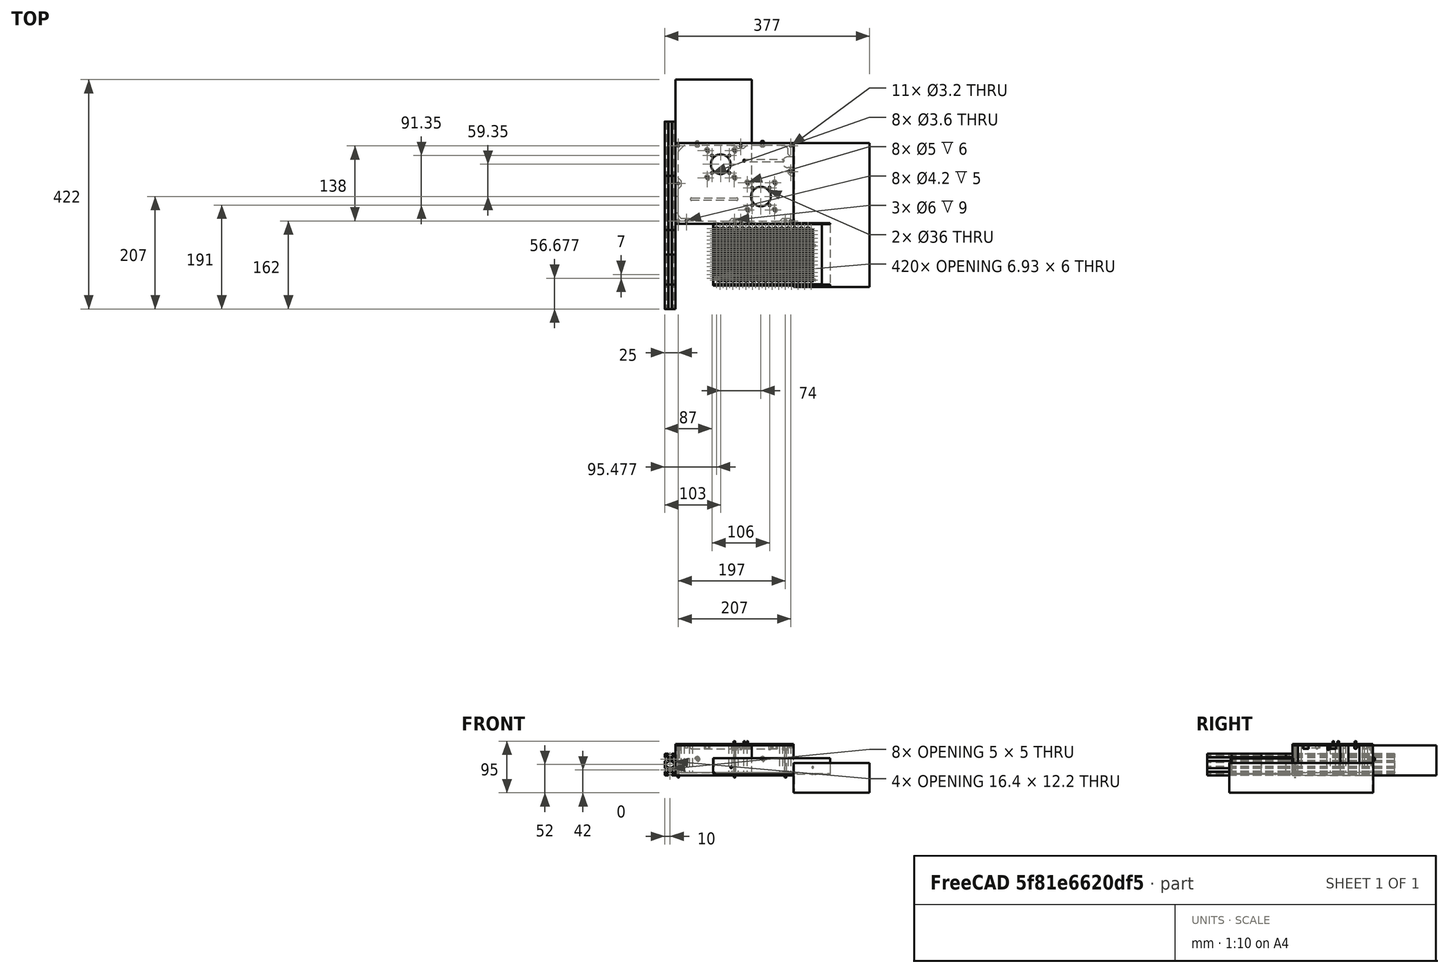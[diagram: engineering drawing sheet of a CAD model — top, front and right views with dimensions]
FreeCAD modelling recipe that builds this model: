
FCSTD DOCUMENT  (FreeCAD 0.19R24291 (Git))
Label: Electronics Enclosure
License: All rights reserved
LicenseURL: http://en.wikipedia.org/wiki/All_rights_reserved
objects: Mesh::Feature×26, Sketcher::SketchObject×10, Part::FeaturePython×10, App::DocumentObjectGroup×6, PartDesign::Pad×5, PartDesign::Pocket×5, Part::Feature×5, PartDesign::Body×3, PartDesign::ShapeBinder×1, Part::Thickness×1, PartDesign::Fillet×1, App::LinkGroup×1
note: 52 computed .brp shape members not serialized (recipe doc carries the construction recipe); baked Part::Feature solids carry a one-line shape summary decoded from their .brp

FEATURE [Sketcher::SketchObject] Sketch
  FullyConstrained = true
  MapMode = 5
  Support = -> [XY_Plane]
  sketch-geometry (8):
    g0: LineSegment StartX=0 StartY=0 StartZ=0 EndX=217 EndY=0 EndZ=0
    g1: LineSegment StartX=217 StartY=0 StartZ=0 EndX=217 EndY=103 EndZ=0
    g2: LineSegment StartX=217 StartY=148 StartZ=0 EndX=0 EndY=148 EndZ=0
    g3: LineSegment StartX=0 StartY=148 StartZ=0 EndX=0 EndY=0 EndZ=0
    g4: LineSegment StartX=217 StartY=123 StartZ=0 EndX=207 EndY=123 EndZ=0
    g5: LineSegment StartX=217 StartY=103 StartZ=0 EndX=207 EndY=103 EndZ=0
    g6: ArcOfCircle CenterX=207 CenterY=113 CenterZ=0 NormalX=0 NormalY=0 NormalZ=1 AngleXU=0 Radius=10 StartAngle=1.5708 EndAngle=4.71239
    g7: LineSegment StartX=217 StartY=123 StartZ=0 EndX=217 EndY=148 EndZ=0
  constraints (23):
    c: Coincident(g0,g1)
    c: Coincident(g7,g2)
    c: Coincident(g2,g3)
    c: Coincident(g3,g0)
    c: Horizontal(g0)
    c: Horizontal(g2)
    c: Vertical(g1)
    c: Vertical(g3)
    c: Coincident(g0,g-1)
    c: DistanceX(g0,g0) = 217
    c: DistanceY(g3,g3) = 148
    c: Horizontal(g4)
    c: Horizontal(g5)
    c: Coincident(g6,g4)
    c: Coincident(g6,g5)
    c: DistanceY(g5,g4) = 20
    c: Vertical(g4,g6)
    c: Vertical(g6,g5)
    c: DistanceY(g4,g7) = 25
    c: DistanceX(g5,g5) = 10
    c: Coincident(g1,g5)
    c: Coincident(g7,g4)
    c: Tangent(g1,g7)
FEATURE [PartDesign::Pad] Pad  label="Base"
  Direction = (1,1,1)
  Length = 5
  Length2 = 100
  Profile = -> Sketch
  Type = 0
FEATURE [Sketcher::SketchObject] Sketch001
  ExternalGeometry = -> [Pad]
  FullyConstrained = true
  MapMode = 5
  Placement = pos=(0,0,5) rot=(0,0,1;0rad)
  Support = -> [Pad]
  sketch-geometry (14):
    g0: LineSegment StartX=217 StartY=10 StartZ=0 EndX=217 EndY=0 EndZ=0
    g1: LineSegment StartX=217 StartY=0 StartZ=0 EndX=0 EndY=0 EndZ=0
    g2: LineSegment StartX=0 StartY=0 StartZ=0 EndX=0 EndY=148 EndZ=0
    g3: LineSegment StartX=0 StartY=148 StartZ=0 EndX=217 EndY=148 EndZ=0
    g4: LineSegment StartX=217 StartY=148 StartZ=0 EndX=217 EndY=123 EndZ=0
    g5: LineSegment StartX=217 StartY=123 StartZ=0 EndX=207 EndY=123 EndZ=0
    g6: LineSegment StartX=207 StartY=123 StartZ=0 EndX=207 EndY=138 EndZ=0
    g7: LineSegment StartX=207 StartY=138 StartZ=0 EndX=10 EndY=138 EndZ=0
    g8: LineSegment StartX=10 StartY=138 StartZ=0 EndX=10 EndY=10 EndZ=0
    g9: LineSegment StartX=10 StartY=10 StartZ=0 EndX=217 EndY=10 EndZ=0
    g10: LineSegment StartX=217 StartY=103 StartZ=0 EndX=207 EndY=103 EndZ=0
    g11: LineSegment StartX=207 StartY=103 StartZ=0 EndX=207 EndY=88 EndZ=0
    g12: LineSegment StartX=207 StartY=88 StartZ=0 EndX=217 EndY=88 EndZ=0
    g13: LineSegment StartX=217 StartY=88 StartZ=0 EndX=217 EndY=103 EndZ=0
  constraints (35):
    c: PointOnObject(g0,g-6)
    c: Coincident(g0,g-6)
    c: Coincident(g0,g1)
    c: Coincident(g1,g-1)
    c: Coincident(g1,g2)
    c: Coincident(g2,g-4)
    c: Coincident(g2,g3)
    c: Coincident(g3,g-4)
    c: Coincident(g3,g4)
    c: Coincident(g4,g-3)
    c: Coincident(g4,g5)
    c: Coincident(g5,g-3)
    c: Coincident(g5,g6)
    c: Vertical(g6)
    c: Coincident(g6,g7)
    c: Horizontal(g7)
    c: Coincident(g7,g8)
    c: Vertical(g8)
    c: Coincident(g8,g9)
    c: Coincident(g9,g0)
    c: Horizontal(g9)
    c: DistanceY(g0,g0) = 10
    c: DistanceY(g6,g3) = 10
    c: DistanceX(g2,g7) = 10
    c: Coincident(g10,g11)
    c: Coincident(g11,g12)
    c: Coincident(g12,g13)
    c: Coincident(g13,g10)
    c: Horizontal(g10)
    c: Horizontal(g12)
    c: Vertical(g11)
    c: Vertical(g13)
    c: Coincident(g10,g-6)
    c: Vertical(g10,g5)
    c: DistanceY(g13,g13) = 15
FEATURE [PartDesign::Pad] Pad001  label="Walls"
  BaseFeature = -> Pad
  Direction = (1,1,1)
  Length = 50
  Length2 = 100
  Profile = -> Sketch001
  Type = 0
FEATURE [Sketcher::SketchObject] Sketch002
  ExternalGeometry = -> [Pad001]
  FullyConstrained = true
  MapMode = 5
  Placement = pos=(0,0,55) rot=(0,0,1;0rad)
  Support = -> [Pad001]
  sketch-geometry (3):
    g0: Circle CenterX=5 CenterY=5 CenterZ=0 NormalX=0 NormalY=0 NormalZ=1 AngleXU=0 Radius=1.6
    g1: Circle CenterX=108.5 CenterY=5 CenterZ=0 NormalX=0 NormalY=0 NormalZ=1 AngleXU=0 Radius=1.6
    g2: Circle CenterX=202 CenterY=5 CenterZ=0 NormalX=0 NormalY=0 NormalZ=1 AngleXU=0 Radius=1.6
  constraints (10):
    c: Horizontal(g0,g1)
    c: Horizontal(g1,g2)
    c: Radius(g0) = 1.6
    c: Equal(g0,g1)
    c: Equal(g1,g2)
    c: DistanceY(g-1,g0) = 5
    c: DistanceX(g-1,g0) = 5
    c: DistanceX(g2,g-3) = 5
    c: DistanceX(g-1,g1) = 108.5
    c: DistanceX(g1,g-3) = 98.5
FEATURE [PartDesign::Pocket] Pocket  label="Center mounting holes"
  BaseFeature = -> Pad001
  Length = 55
  Length2 = 100
  Profile = -> Sketch002
  Type = 0
FEATURE [Sketcher::SketchObject] Sketch003
  ExternalGeometry = -> [Pocket]
  FullyConstrained = true
  MapMode = 5
  Placement = pos=(0,0,55) rot=(0,0,1;0rad)
  Support = -> [Pocket]
  sketch-geometry (3):
    g0: Circle CenterX=5 CenterY=5 CenterZ=0 NormalX=0 NormalY=0 NormalZ=1 AngleXU=0 Radius=3
    g1: Circle CenterX=108.5 CenterY=5 CenterZ=0 NormalX=0 NormalY=0 NormalZ=1 AngleXU=0 Radius=3
    g2: Circle CenterX=202 CenterY=5 CenterZ=0 NormalX=0 NormalY=0 NormalZ=1 AngleXU=0 Radius=3
  constraints (6):
    c: Coincident(g0,g-3)
    c: Coincident(g1,g-4)
    c: Coincident(g2,g-5)
    c: Radius(g0) = 3
    c: Equal(g0,g1)
    c: Equal(g1,g2)
FEATURE [PartDesign::Pocket] Pocket001  label="Center Recess"
  BaseFeature = -> Pocket
  Length = 9
  Length2 = 100
  Profile = -> Sketch003
  Type = 0
FEATURE [Mesh::Feature] _040_Profile___200mm  label="4040_Profile_-_200mm"
  Placement = pos=(8.9e-15,148,40) rot=(0,1,0;1.5708rad)
FEATURE [Sketcher::SketchObject] Sketch004
  FullyConstrained = true
  MapMode = 5
  Placement = pos=(0,138,0) rot=(1,0,0;1.5708rad)
  Support = -> [Pocket001]
  sketch-geometry (2):
    g0: Circle CenterX=40 CenterY=30 CenterZ=0 NormalX=0 NormalY=0 NormalZ=1 AngleXU=0 Radius=2.6
    g1: Circle CenterX=160 CenterY=30 CenterZ=0 NormalX=0 NormalY=0 NormalZ=1 AngleXU=0 Radius=2.6
  constraints (6):
    c: Radius(g0) = 2.6
    c: Equal(g0,g1)
    c: Horizontal(g1,g0)
    c: DistanceY(g-1,g0) = 30
    c: DistanceX(g-1,g0) = 40
    c: DistanceX(g0,g1) = 120
FEATURE [PartDesign::Pocket] Pocket002  label="Mounting Holes Outside"
  BaseFeature = -> Pocket001
  Length = 10
  Length2 = 100
  Profile = -> Sketch004
  Type = 0
FEATURE [Mesh::Feature] _040_Profile___200mm001  label="4040_Profile_-_200mm001"
  Placement = pos=(-43,-5,9e-16) rot=(0,1,0;1.5708rad)
FEATURE [Mesh::Feature] _040_Profile___200mm002  label="4040_Profile_-_200mm002"
  Placement = pos=(157,-157,40) rot=(0,1,0;1.5708rad)
FEATURE [Mesh::Feature] _040_Profile___200mm003  label="4040_Profile_-_200mm003"
  Placement = pos=(157,-5,9e-16) rot=(0,1,0;1.5708rad)
FEATURE [Part::Feature] Part__Feature  label="2040 Extrusion"
  Placement = pos=(-10,88,20) rot=(0.57735,-0.57735,0.57735;2.0944rad)
  shape: bbox 20 x 100 x 40 mm, 138 faces (baked)
FEATURE [Part::Feature] Part__Feature001  label="2040 Extrusion001"
  Placement = pos=(-10,-12,20) rot=(0.57735,-0.57735,0.57735;2.0944rad)
  shape: bbox 20 x 100 x 40 mm, 138 faces (baked)
FEATURE [Sketcher::SketchObject] Sketch005
  ExternalGeometry = -> [Pocket002]
  FullyConstrained = true
  MapMode = 5
  Placement = pos=(0,0,55) rot=(0,0,1;0rad)
  Support = -> [Pocket002]
  sketch-geometry (12):
    g0: LineSegment StartX=0 StartY=20 StartZ=0 EndX=10 EndY=20 EndZ=0
    g1: LineSegment StartX=10 StartY=20 StartZ=0 EndX=10 EndY=50 EndZ=0
    g2: LineSegment StartX=10 StartY=50 StartZ=0 EndX=0 EndY=50 EndZ=0
    g3: LineSegment StartX=0 StartY=50 StartZ=0 EndX=0 EndY=20 EndZ=0
    g4: Circle CenterX=5 CenterY=74 CenterZ=0 NormalX=0 NormalY=0 NormalZ=1 AngleXU=0 Radius=2.1
    g5: Circle CenterX=5 CenterY=143 CenterZ=0 NormalX=0 NormalY=0 NormalZ=1 AngleXU=0 Radius=2.1
    g6: Circle CenterX=20 CenterY=5 CenterZ=0 NormalX=0 NormalY=0 NormalZ=1 AngleXU=0 Radius=2.1
    g7: Circle CenterX=212 CenterY=5 CenterZ=0 NormalX=0 NormalY=0 NormalZ=1 AngleXU=0 Radius=2.1
    g8: Circle CenterX=120 CenterY=5 CenterZ=0 NormalX=0 NormalY=0 NormalZ=1 AngleXU=0 Radius=2.1
    g9: Circle CenterX=212 CenterY=95.5 CenterZ=0 NormalX=0 NormalY=0 NormalZ=1 AngleXU=0 Radius=2.1
    g10: Circle CenterX=212 CenterY=143 CenterZ=0 NormalX=0 NormalY=0 NormalZ=1 AngleXU=0 Radius=2.1
    g11: Circle CenterX=120 CenterY=143 CenterZ=0 NormalX=0 NormalY=0 NormalZ=1 AngleXU=0 Radius=2.1
  constraints (36):
    c: Coincident(g0,g1)
    c: Coincident(g1,g2)
    c: Coincident(g2,g3)
    c: Coincident(g3,g0)
    c: Horizontal(g0)
    c: Horizontal(g2)
    c: Vertical(g1)
    c: Vertical(g3)
    c: PointOnObject(g0,g-2)
    c: PointOnObject(g1,g-3)
    c: DistanceY(g-1,g0) = 20
    c: DistanceY(g3,g3) = 30
    c: Radius(g5) = 2.1
    c: Equal(g5,g4)
    c: Equal(g5,g6)
    c: Equal(g5,g8)
    c: Equal(g5,g7)
    c: Equal(g5,g9)
    c: Equal(g5,g10)
    c: Equal(g5,g11)
    c: Vertical(g4,g5)
    c: Horizontal(g6,g8)
    c: Horizontal(g8,g7)
    c: Vertical(g7,g9)
    c: Vertical(g9,g10)
    c: Horizontal(g10,g11)
    c: Horizontal(g11,g5)
    c: DistanceX(g-1,g5) = 5
    c: DistanceY(g-3,g5) = 5
    c: DistanceY(g6,g-3) = 5
    c: DistanceX(g-1,g6) = 20
    c: DistanceX(g7,g-4) = 5
    c: DistanceX(g6,g8) = 100
    c: Vertical(g8,g11)
    c: DistanceY(g9,g-6) = 7.5
    c: DistanceY(g-1,g4) = 74
FEATURE [PartDesign::Pocket] Pocket003  label="Top Mounting and Recess"
  BaseFeature = -> Pocket002
  Length = 5
  Length2 = 12
  Profile = -> Sketch005
  Type = 0
FEATURE [Mesh::Feature] DIN_Rail_No_Interlocks
  Placement = pos=(12,58,5) rot=(0.57735,-0.57735,0.57735;4.18879rad)
FEATURE [Mesh::Feature] DIN_Rail_No_Interlocks001
  Placement = pos=(82,58,5) rot=(0.57735,-0.57735,0.57735;4.18879rad)
FEATURE [Mesh::Feature] DIN_Rail_No_Interlocks002
  Placement = pos=(142,58,5) rot=(0.57735,-0.57735,0.57735;4.18879rad)
FEATURE [Sketcher::SketchObject] Sketch007
  ExternalGeometry = -> [Pocket003]
  FullyConstrained = true
  MapMode = 5
  Placement = pos=(0,0,55) rot=(0,0,1;0rad)
  Support = -> [Pocket003]
  sketch-geometry (33):
    g0: LineSegment StartX=10 StartY=138 StartZ=0 EndX=4 EndY=132 EndZ=0
    g1: LineSegment StartX=4 StartY=132 StartZ=0 EndX=4 EndY=85 EndZ=0
    g2: LineSegment StartX=4 StartY=85 StartZ=0 EndX=10 EndY=79 EndZ=0
    g3: LineSegment StartX=10 StartY=79 StartZ=0 EndX=10 EndY=138 EndZ=0
    g4: LineSegment StartX=25 StartY=10 StartZ=0 EndX=103.5 EndY=10 EndZ=0
    g5: LineSegment StartX=103.5 StartY=10 StartZ=0 EndX=97.5 EndY=4 EndZ=0
    g6: LineSegment StartX=97.5 StartY=4 StartZ=0 EndX=31 EndY=4 EndZ=0
    g7: LineSegment StartX=31 StartY=4 StartZ=0 EndX=25 EndY=10 EndZ=0
    g8: LineSegment StartX=125 StartY=10 StartZ=0 EndX=197 EndY=10 EndZ=0
    g9: LineSegment StartX=197 StartY=10 StartZ=0 EndX=191 EndY=4 EndZ=0
    g10: LineSegment StartX=191 StartY=4 StartZ=0 EndX=131 EndY=4 EndZ=0
    g11: LineSegment StartX=131 StartY=4 StartZ=0 EndX=125 EndY=10 EndZ=0
    g12: LineSegment StartX=10 StartY=138 StartZ=0 EndX=115 EndY=138 EndZ=0
    g13: LineSegment StartX=115 StartY=138 StartZ=0 EndX=109 EndY=144 EndZ=0
    g14: LineSegment StartX=109 StartY=144 StartZ=0 EndX=16 EndY=144 EndZ=0
    g15: LineSegment StartX=16 StartY=144 StartZ=0 EndX=10 EndY=138 EndZ=0
    g16: LineSegment StartX=125 StartY=138 StartZ=0 EndX=207 EndY=138 EndZ=0
    g17: LineSegment StartX=207 StartY=138 StartZ=0 EndX=201 EndY=144 EndZ=0
    g18: LineSegment StartX=201 StartY=144 StartZ=0 EndX=131 EndY=144 EndZ=0
    g19: LineSegment StartX=131 StartY=144 StartZ=0 EndX=125 EndY=138 EndZ=0
    g20: LineSegment StartX=10 StartY=69 StartZ=0 EndX=4 EndY=63 EndZ=0
    g21: LineSegment StartX=4 StartY=63 StartZ=0 EndX=4 EndY=16 EndZ=0
    g22: LineSegment StartX=4 StartY=16 StartZ=0 EndX=10 EndY=10 EndZ=0
    g23: LineSegment StartX=10 StartY=10 StartZ=0 EndX=10 EndY=69 EndZ=0
    g24: LineSegment StartX=207 StartY=128 StartZ=0 EndX=212 EndY=123 EndZ=0
    g25: LineSegment StartX=212 StartY=123 StartZ=0 EndX=207 EndY=123 EndZ=0
    g26: LineSegment StartX=207 StartY=123 StartZ=0 EndX=207 EndY=128 EndZ=0
    g27: LineSegment StartX=212 StartY=103 StartZ=0 EndX=207 EndY=98 EndZ=0
    g28: LineSegment StartX=207 StartY=98 StartZ=0 EndX=207 EndY=103 EndZ=0
    g29: LineSegment StartX=207 StartY=103 StartZ=0 EndX=212 EndY=103 EndZ=0
    g30: LineSegment StartX=212 StartY=88 StartZ=0 EndX=207 EndY=93 EndZ=0
    g31: LineSegment StartX=207 StartY=93 StartZ=0 EndX=207 EndY=88 EndZ=0
    g32: LineSegment StartX=207 StartY=88 StartZ=0 EndX=212 EndY=88 EndZ=0
  constraints (92):
    c: Coincident(g0,g1)
    c: Coincident(g1,g2)
    c: Coincident(g2,g3)
    c: Coincident(g3,g0)
    c: Vertical(g1)
    c: Vertical(g3)
    c: Coincident(g4,g5)
    c: Coincident(g5,g6)
    c: Coincident(g6,g7)
    c: Coincident(g7,g4)
    c: Horizontal(g4)
    c: Horizontal(g6)
    c: Coincident(g8,g9)
    c: Coincident(g9,g10)
    c: Coincident(g10,g11)
    c: Coincident(g11,g8)
    c: Horizontal(g8)
    c: Horizontal(g10)
    c: Coincident(g12,g13)
    c: Coincident(g13,g14)
    c: Coincident(g14,g15)
    c: Coincident(g15,g12)
    c: Horizontal(g12)
    c: Horizontal(g14)
    c: Coincident(g16,g17)
    c: Coincident(g17,g18)
    c: Coincident(g18,g19)
    c: Coincident(g19,g16)
    c: Horizontal(g16)
    c: Horizontal(g18)
    c: DistanceX(g0,g0) = 6
    c: Coincident(g20,g21)
    c: Coincident(g21,g22)
    c: Coincident(g22,g23)
    c: Coincident(g23,g20)
    c: Vertical(g21)
    c: Vertical(g23)
    c: PointOnObject(g8,g-3)
    c: DistanceX(g-7,g8) = 5
    c: Angle(g10,g11) = 2.35619
    c: Angle(g9,g10) = 2.35619
    c: DistanceY(g-1,g9) = 4
    c: DistanceX(g8,g-8) = 5
    c: PointOnObject(g4,g-3)
    c: Angle(g6,g7) = 2.35619
    c: Angle(g5,g6) = 2.35619
    c: Horizontal(g5,g10)
    c: DistanceX(g4,g-6) = 5
    c: DistanceX(g-5,g4) = 5
    c: Angle(g22,g21) = 2.35619
    c: Angle(g21,g20) = 2.35619
    c: DistanceX(g20,g20) = 6
    c: DistanceY(g20,g-10) = 5
    c: Angle(g1,g0) = 2.35619
    c: Angle(g2,g1) = 2.35619
    c: DistanceY(g-10,g2) = 5
    c: Coincident(g0,g-11)
    c: Angle(g15,g14) = 2.35619
    c: Angle(g14,g13) = 2.35619
    c: DistanceY(g12,g14) = 6
    c: Coincident(g12,g0)
    c: DistanceX(g12,g-13) = 5
    c: Angle(g19,g18) = 2.35619
    c: Angle(g18,g17) = 2.35619
    c: Horizontal(g13,g18)
    c: DistanceX(g-13,g16) = 5
    c: Coincident(g16,g-12)
    c: PointOnObject(g24,g-17)
    c: PointOnObject(g24,g-16)
    c: Coincident(g24,g25)
    c: Coincident(g25,g-17)
    c: Coincident(g25,g26)
    c: Coincident(g26,g24)
    c: DistanceX(g25,g25) = 5
    c: Equal(g25,g26)
    c: PointOnObject(g27,g-14)
    c: Coincident(g27,g28)
    c: Coincident(g28,g-14)
    c: Vertical(g28)
    c: Coincident(g28,g29)
    c: Coincident(g29,g27)
    c: PointOnObject(g30,g-15)
    c: Coincident(g30,g31)
    c: Coincident(g31,g-15)
    c: Coincident(g31,g32)
    c: Coincident(g32,g30)
    c: Vertical(g31)
    c: Equal(g25,g29)
    c: Equal(g29,g28)
    c: Equal(g28,g31)
    c: Equal(g31,g32)
    c: Coincident(g22,g-9)
FEATURE [PartDesign::Pocket] Pocket004  label="Wall Cutouts"
  BaseFeature = -> Pocket003
  Length = 50
  Length2 = 100
  Profile = -> Sketch007
  Type = 0
FEATURE [PartDesign::Body] Body  label="Main Enclosure"
  Group = -> [Sketch,Pad,Sketch001,Pad001,Sketch002,Pocket,Sketch003,Pocket001,Sketch004,Pocket002,Sketch005,Pocket003,Sketch007,Pocket004]
  Origin = -> Origin
  Tip = -> Pocket004
FEATURE [Part::FeaturePython] Screw  label="M3x50-Screw"  # Fasteners workbench fastener (typed FeaturePython)
  Placement = pos=(5,5,46) rot=(0,0,1;0rad)
  baseObject = -> Body [Edge43]
  diameter = 4
  invert = false
  length = 10
  lengthCustom = 50
  matchOuter = false
  offset = 0
  thread = false
  type = 33
FEATURE [Part::FeaturePython] Screw001  label="M3x50-Screw063"  # Fasteners workbench fastener (typed FeaturePython)
  Placement = pos=(108.5,5,46) rot=(0,0,1;0rad)
  baseObject = -> Body [Edge41]
  diameter = 4
  invert = false
  length = 10
  lengthCustom = 50
  matchOuter = false
  offset = 0
  thread = false
  type = 33
FEATURE [Part::FeaturePython] Screw005  label="M5x8-Screw001"  # Fasteners workbench fastener (typed FeaturePython)
  Placement = pos=(40,144,30) rot=(1,0,0;1.5708rad)
  baseObject = -> Body [Edge93]
  diameter = 3
  invert = false
  length = 12
  lengthCustom = 8
  matchOuter = false
  offset = 0
  thread = false
  type = 39
FEATURE [Part::Feature] Part__Feature002  label="2040 Extrusion002"
  Placement = pos=(-10,-112,20) rot=(0.57735,-0.57735,0.57735;2.0944rad)
  shape: bbox 20 x 100 x 40 mm, 138 faces (baked)
FEATURE [Part::Feature] Part__Feature003  label="2040 Extrusion003"
  Placement = pos=(-10,-157,20) rot=(0.57735,-0.57735,0.57735;2.0944rad)
  shape: bbox 20 x 100 x 40 mm, 138 faces (baked)
FEATURE [Mesh::Feature] _040_Profile___200mm004  label="4040_Profile_-_200mm004"
  Placement = pos=(8.9e-15,-157,40) rot=(0,1,0;1.5708rad)
FEATURE [Mesh::Feature] _040_Profile___200mm005  label="4040_Profile_-_200mm005"
  Placement = pos=(157,148,40) rot=(0,1,0;1.5708rad)
FEATURE [Part::Feature] Part__Feature1009  label="Meanwell"
  Placement = pos=(198.3,166.3,-8) rot=(0,0,1;3.14159rad)
  shape: bbox 215 x 115 x 30 mm, 2574 faces (baked)
FEATURE [Mesh::Feature] pcb_din_clip_x3
  Placement = pos=(168,-92,-133.5) rot=(0,-1,0;1.5708rad)
FEATURE [Mesh::Feature] Nanopi_M1_Din_Rail_Mount  label="Nanopi M1 Din Rail Mount"
  Placement = pos=(163,58,25.5) rot=(0,0,1;0rad)
FEATURE [App::DocumentObjectGroup] Group  label="Electronics"
  Group = -> [pcb_din_clip_x3,Nanopi_M1_Din_Rail_Mount,DIN_Rail_No_Interlocks,DIN_Rail_No_Interlocks001,DIN_Rail_No_Interlocks002]
FEATURE [Mesh::Feature] Grill_V2_Spacer___4mm  label="Grill V2-Spacer - 4mm"
  Placement = pos=(-23,-181,245) rot=(0,1,0;1.5708rad)
FEATURE [Mesh::Feature] Grill_V2_Spacer___4mm001  label="Grill V2-Spacer - 4mm001"
  Placement = pos=(-23,212,-205) rot=(0.707107,0,0.707107;3.14159rad)
FEATURE [Mesh::Feature] Middle_Grill_V2  label="Middle Grill V2"
  Placement = pos=(-20,-57,64) rot=(-0.57735,-0.57735,0.57735;2.0944rad)
FEATURE [Mesh::Feature] grill_front_left
  Placement = pos=(-23,-212,140) rot=(0.57735,0.57735,-0.57735;4.18879rad)
FEATURE [Mesh::Feature] grill_front_right
  Placement = pos=(-23,24,140) rot=(0.57735,0.57735,-0.57735;4.18879rad)
FEATURE [Mesh::Feature] _a__grill_endcap_x4  label="[a]_grill_endcap_x4"
  Placement = pos=(-39,58,-80) rot=(0,1,0;4.71239rad)
FEATURE [Mesh::Feature] _a__y_idler_outter  label="[a]_y_idler_outter"
  Placement = pos=(-43,-95,92) rot=(0.57735,0.57735,-0.57735;4.18879rad)
FEATURE [App::DocumentObjectGroup] Group001  label="Profiles"
  Group = -> [Part__Feature002,Part__Feature003,_040_Profile___200mm004,_040_Profile___200mm005,_040_Profile___200mm,_040_Profile___200mm001,_040_Profile___200mm002,_040_Profile___200mm003,Part__Feature,Part__Feature001,_a__y_idler_outter]
FEATURE [Mesh::Feature] _a__grill_endcap_x005  label="[a]_grill_endcap_x005"
  Placement = pos=(-39,-246,-80) rot=(0,1,0;4.71239rad)
FEATURE [Part::FeaturePython] Screw006  label="M3x50-Screw064"  # Fasteners workbench fastener (typed FeaturePython)
  Placement = pos=(202,5,46) rot=(0,0,1;0rad)
  baseObject = -> Body [Edge47]
  diameter = 4
  invert = false
  length = 10
  lengthCustom = 50
  matchOuter = false
  offset = 0
  thread = false
  type = 33
FEATURE [Part::FeaturePython] Screw007  label="M5x8-Screw"  # Fasteners workbench fastener (typed FeaturePython)
  Placement = pos=(160,144,30) rot=(1,0,0;1.5708rad)
  baseObject = -> Body [Edge95]
  diameter = 3
  invert = false
  length = 12
  lengthCustom = 8
  matchOuter = false
  offset = 0
  thread = false
  type = 39
FEATURE [App::DocumentObjectGroup] Group003  label="Screws"
  Group = -> [Screw,Screw001,Screw005,Screw006,Screw007]
FEATURE [PartDesign::ShapeBinder] ShapeBinder
  Support = -> [Pocket004]
  TraceSupport = false
FEATURE [Sketcher::SketchObject] Sketch008
  ExternalGeometry = -> [ShapeBinder]
  FullyConstrained = true
  MapMode = 5
  Support = -> [XY_Plane001]
  sketch-geometry (50):
    g0: LineSegment StartX=0 StartY=0 StartZ=0 EndX=217 EndY=0 EndZ=0
    g1: LineSegment StartX=217 StartY=0 StartZ=0 EndX=217 EndY=148 EndZ=0
    g2: LineSegment StartX=217 StartY=148 StartZ=0 EndX=0 EndY=148 EndZ=0
    g3: LineSegment StartX=0 StartY=148 StartZ=0 EndX=0 EndY=0 EndZ=0
    g4: Circle CenterX=5 CenterY=74 CenterZ=0 NormalX=0 NormalY=0 NormalZ=1 AngleXU=0 Radius=1.6
    g5: Circle CenterX=5 CenterY=143 CenterZ=0 NormalX=0 NormalY=0 NormalZ=1 AngleXU=0 Radius=1.6
    g6: Circle CenterX=120 CenterY=143 CenterZ=0 NormalX=0 NormalY=0 NormalZ=1 AngleXU=0 Radius=1.6
    g7: Circle CenterX=212 CenterY=143 CenterZ=0 NormalX=0 NormalY=0 NormalZ=1 AngleXU=0 Radius=1.6
    g8: Circle CenterX=212 CenterY=95.5 CenterZ=0 NormalX=0 NormalY=0 NormalZ=1 AngleXU=0 Radius=1.6
    g9: Circle CenterX=212 CenterY=5 CenterZ=0 NormalX=0 NormalY=0 NormalZ=1 AngleXU=0 Radius=1.6
    g10: Circle CenterX=120 CenterY=5 CenterZ=0 NormalX=0 NormalY=0 NormalZ=1 AngleXU=0 Radius=1.6
    g11: Circle CenterX=20 CenterY=5 CenterZ=0 NormalX=0 NormalY=0 NormalZ=1 AngleXU=0 Radius=1.6
    g12: LineSegment StartX=63 StartY=130 StartZ=0 EndX=103 EndY=130 EndZ=0
    g13: LineSegment StartX=103 StartY=130 StartZ=0 EndX=103 EndY=90 EndZ=0
    g14: LineSegment StartX=103 StartY=90 StartZ=0 EndX=63 EndY=90 EndZ=0
    g15: LineSegment StartX=63 StartY=90 StartZ=0 EndX=63 EndY=130 EndZ=0
    g16: Circle CenterX=58 CenterY=134.35 CenterZ=0 NormalX=0 NormalY=0 NormalZ=1 AngleXU=0 Radius=1.6
    g17: Circle CenterX=108 CenterY=134.35 CenterZ=0 NormalX=0 NormalY=0 NormalZ=1 AngleXU=0 Radius=1.6
    g18: LineSegment StartX=58 StartY=134.35 StartZ=0 EndX=108 EndY=134.35 EndZ=0
    g19: Circle CenterX=58 CenterY=84.35 CenterZ=0 NormalX=0 NormalY=0 NormalZ=1 AngleXU=0 Radius=1.6
    g20: LineSegment StartX=58 StartY=134.35 StartZ=0 EndX=58 EndY=84.35 EndZ=0
    g21: Circle CenterX=108 CenterY=84.35 CenterZ=0 NormalX=0 NormalY=0 NormalZ=1 AngleXU=0 Radius=1.6
    g22: LineSegment StartX=58 StartY=84.35 StartZ=0 EndX=108 EndY=84.35 EndZ=0
    g23: Circle CenterX=83 CenterY=109.35 CenterZ=0 NormalX=0 NormalY=0 NormalZ=1 AngleXU=0 Radius=18
    g24: LineSegment StartX=137 StartY=70.65 StartZ=0 EndX=177 EndY=70.65 EndZ=0
    g25: LineSegment StartX=177 StartY=70.65 StartZ=0 EndX=177 EndY=30.65 EndZ=0
    g26: LineSegment StartX=177 StartY=30.65 StartZ=0 EndX=137 EndY=30.65 EndZ=0
    g27: LineSegment StartX=137 StartY=30.65 StartZ=0 EndX=137 EndY=70.65 EndZ=0
    g28: Circle CenterX=132 CenterY=75 CenterZ=0 NormalX=0 NormalY=0 NormalZ=1 AngleXU=0 Radius=1.6
    g29: Circle CenterX=182 CenterY=75 CenterZ=0 NormalX=0 NormalY=0 NormalZ=1 AngleXU=0 Radius=1.6
    g30: LineSegment StartX=132 StartY=75 StartZ=0 EndX=182 EndY=75 EndZ=0
    g31: Circle CenterX=132 CenterY=25 CenterZ=0 NormalX=0 NormalY=0 NormalZ=1 AngleXU=0 Radius=1.6
    g32: LineSegment StartX=132 StartY=75 StartZ=0 EndX=132 EndY=25 EndZ=0
    g33: Circle CenterX=182 CenterY=25 CenterZ=0 NormalX=0 NormalY=0 NormalZ=1 AngleXU=0 Radius=1.6
    g34: LineSegment StartX=132 StartY=25 StartZ=0 EndX=182 EndY=25 EndZ=0
    g35: Circle CenterX=157 CenterY=50 CenterZ=0 NormalX=0 NormalY=0 NormalZ=1 AngleXU=0 Radius=18
    g36: Circle CenterX=67 CenterY=125.35 CenterZ=0 NormalX=0 NormalY=0 NormalZ=1 AngleXU=0 Radius=1.8
    g37: Circle CenterX=99 CenterY=125.35 CenterZ=0 NormalX=0 NormalY=0 NormalZ=1 AngleXU=0 Radius=1.8
    g38: LineSegment StartX=67 StartY=125.35 StartZ=0 EndX=99 EndY=125.35 EndZ=0
    g39: Circle CenterX=67 CenterY=93.35 CenterZ=0 NormalX=0 NormalY=0 NormalZ=1 AngleXU=0 Radius=1.8
    g40: LineSegment StartX=67 StartY=125.35 StartZ=0 EndX=67 EndY=93.35 EndZ=0
    g41: Circle CenterX=99 CenterY=93.35 CenterZ=0 NormalX=0 NormalY=0 NormalZ=1 AngleXU=0 Radius=1.8
    g42: LineSegment StartX=67 StartY=93.35 StartZ=0 EndX=99 EndY=93.35 EndZ=0
    g43: Circle CenterX=141 CenterY=66 CenterZ=0 NormalX=0 NormalY=0 NormalZ=1 AngleXU=0 Radius=1.8
    g44: Circle CenterX=173 CenterY=66 CenterZ=0 NormalX=0 NormalY=0 NormalZ=1 AngleXU=0 Radius=1.8
    g45: LineSegment StartX=141 StartY=66 StartZ=0 EndX=173 EndY=66 EndZ=0
    g46: Circle CenterX=141 CenterY=34 CenterZ=0 NormalX=0 NormalY=0 NormalZ=1 AngleXU=0 Radius=1.8
    g47: LineSegment StartX=141 StartY=66 StartZ=0 EndX=141 EndY=34 EndZ=0
    g48: Circle CenterX=173 CenterY=34 CenterZ=0 NormalX=0 NormalY=0 NormalZ=1 AngleXU=0 Radius=1.8
    g49: LineSegment StartX=141 StartY=34 StartZ=0 EndX=173 EndY=34 EndZ=0
  constraints (120):
    c: Coincident(g0,g1)
    c: Coincident(g1,g2)
    c: Coincident(g2,g3)
    c: Coincident(g3,g0)
    c: Horizontal(g0)
    c: Horizontal(g2)
    c: Vertical(g1)
    c: Vertical(g3)
    c: Coincident(g0,g-1)
    c: DistanceY(g1,g1) = 148
    c: DistanceX(g2,g2) = 217
    c: Coincident(g4,g-10)
    c: Coincident(g5,g-3)
    c: Coincident(g6,g-4)
    c: Coincident(g7,g-5)
    c: Coincident(g8,g-6)
    c: Coincident(g9,g-7)
    c: Coincident(g10,g-8)
    c: Coincident(g11,g-9)
    c: Radius(g5) = 1.6
    c: Equal(g5, g6-g11) x6
    c: Equal(g5,g4)
    c: Coincident(g12,g13)
    c: Coincident(g13,g14)
    c: Coincident(g14,g15)
    c: Coincident(g15,g12)
    c: Horizontal(g12)
    c: Horizontal(g14)
    c: Vertical(g13)
    c: Vertical(g15)
    c: DistanceX(g14,g14) = 40
    c: DistanceY(g15,g15) = 40
    c: DistanceY(g12,g2) = 18
    c: DistanceX(g2,g12) = 63
    c: Coincident(g16,g18)
    c: Coincident(g17,g18)
    c: Distance(g18) = 50
    c: Angle(g18) = 0
    c: Coincident(g16,g20)
    c: Coincident(g19,g20)
    c: Equal(g20,g18)
    c: Perpendicular(g20,g18)
    c: Coincident(g19,g22)
    c: Coincident(g21,g22)
    c: Equal(g18,g22)
    c: Parallel(g22,g18)
    c: Radius(g16) = 1.6
    c: Equal(g16,g17)
    c: Equal(g17,g21)
    c: Equal(g21,g19)
    c: Symmetric(g19,g17,g23)
    c: Radius(g23) = 18
    c: DistanceY(g12,g16) = 4.35
    c: DistanceX(g16,g12) = 5
    c: Coincident(g24,g25)
    c: Coincident(g25,g26)
    c: Coincident(g26,g27)
    c: Coincident(g27,g24)
    c: Horizontal(g24)
    c: Horizontal(g26)
    c: Vertical(g25)
    c: Vertical(g27)
    c: Equal(g14,g26) = 40
    c: Equal(g15,g27) = 40
    c: Coincident(g28,g30)
    c: Coincident(g29,g30)
    c: Equal(g18,g30) = 50
    c: Parallel(g18,g30)
    c: Coincident(g28,g32)
    c: Coincident(g31,g32)
    c: Equal(g32,g30)
    c: Perpendicular(g32,g30)
    c: Coincident(g31,g34)
    c: Coincident(g33,g34)
    c: Equal(g30,g34)
    c: Parallel(g34,g30)
    c: Equal(g16,g28) = 1.6
    c: Equal(g28,g29)
    c: Equal(g29,g33)
    c: Equal(g33,g31)
    c: Symmetric(g31,g29,g35)
    c: Equal(g23,g35) = 18
    c: DistanceY(g24,g28) = 4.35
    c: DistanceX(g28,g24) = 5
    c: DistanceX(g35,g0) = 60
    c: DistanceY(g0,g35) = 50
    c: Radius(g36) = 1.8
    c: Radius(g37) = 1.8
    c: Coincident(g36,g38)
    c: Coincident(g37,g38)
    c: Distance(g38) = 32
    c: Angle(g38) = 0
    c: Radius(g39) = 1.8
    c: Coincident(g36,g40)
    c: Coincident(g39,g40)
    c: Equal(g40,g38)
    c: Perpendicular(g40,g38)
    c: Radius(g41) = 1.8
    c: Coincident(g39,g42)
    c: Coincident(g41,g42)
    c: Equal(g38,g42)
    c: Parallel(g42,g38)
    c: Symmetric(g39,g37,g23)
    c: Equal(g36,g43)
    c: Coincident(g43,g45)
    c: Coincident(g44,g45)
    c: Distance(g45) = 32
    c: Angle(g45) = 0
    c: Coincident(g43,g47)
    c: Coincident(g46,g47)
    c: Equal(g47,g45)
    c: Perpendicular(g47,g45)
    c: Coincident(g46,g49)
    c: Coincident(g48,g49)
    c: Equal(g45,g49)
    c: Parallel(g49,g45)
    c: Symmetric(g43,g48,g35)
    c: Equal(g46,g48)
    c: Equal(g48,g44)
    c: Equal(g44,g43)
FEATURE [PartDesign::Pad] Pad002
  Direction = (1,1,1)
  Length = 3
  Length2 = 100
  Profile = -> Sketch008
  Type = 0
FEATURE [Mesh::Feature] Foot_Extension  label="Foot Extension"
  Placement = pos=(20,168,40) rot=(0,0,1;0rad)
FEATURE [Mesh::Feature] Foot_Extension001  label="Foot Extension001"
  Placement = pos=(335,168,40) rot=(0,0,1;0rad)
FEATURE [Mesh::Feature] Foot_Extension002  label="Foot Extension002"
  Placement = pos=(335,-137,40) rot=(0,0,1;0rad)
FEATURE [Mesh::Feature] Foot_Extension003  label="Foot Extension003"
  Placement = pos=(20,-137,40) rot=(0,0,1;0rad)
FEATURE [App::DocumentObjectGroup] Group002  label="Skirt"
  Group = -> [grill_front_right,grill_front_left,Middle_Grill_V2,Grill_V2_Spacer___4mm001,Grill_V2_Spacer___4mm,_a__grill_endcap_x4,_a__grill_endcap_x005,Foot_Extension,Foot_Extension001,Foot_Extension002,Foot_Extension003]
FEATURE [Mesh::Feature] Left_Front_Case_Cover___Bended  label="Left Front Case Cover - Bended"
  Placement = pos=(217,147,22) rot=(0,0,1;3.14159rad)
FEATURE [Sketcher::SketchObject] Sketch009
  FullyConstrained = true
  MapMode = 5
  Support = -> [XY_Plane002]
  sketch-geometry (4):
    g0: LineSegment StartX=0 StartY=0 StartZ=0 EndX=140 EndY=0 EndZ=0
    g1: LineSegment StartX=140 StartY=0 StartZ=0 EndX=140 EndY=265 EndZ=0
    g2: LineSegment StartX=140 StartY=265 StartZ=0 EndX=0 EndY=265 EndZ=0
    g3: LineSegment StartX=0 StartY=265 StartZ=0 EndX=0 EndY=0 EndZ=0
  constraints (11):
    c: Coincident(g0,g1)
    c: Coincident(g1,g2)
    c: Coincident(g2,g3)
    c: Coincident(g3,g0)
    c: Horizontal(g0)
    c: Horizontal(g2)
    c: Vertical(g1)
    c: Vertical(g3)
    c: Coincident(g0,g-1)
    c: DistanceX(g0,g0) = 140
    c: DistanceY(g3,g3) = 265
FEATURE [PartDesign::Pad] Pad003
  Direction = (1,1,1)
  Length = 55
  Length2 = 100
  Profile = -> Sketch009
  Type = 0
FEATURE [Part::Thickness] Thickness
  Faces = -> Pad003 [Face5]
  Intersection = false
  Join = 0
  Mode = 0
  Placement = pos=(217,-116.5,-32) rot=(0,0,1;0rad)
  SelfIntersection = false
  Value = -1
FEATURE [PartDesign::Body] Body002
  Group = -> [Sketch009,Pad003]
  Origin = -> Origin002
  Tip = -> Pad003
FEATURE [Mesh::Feature] Ender_3_Case_Lid_PS_Cover  label="Ender 3 Case Lid PS Cover"
  Placement = pos=(15,-16,-34) rot=(1,0,0;3.14159rad)
FEATURE [Mesh::Feature] Ender_3_Case_Lid_PS_Cover001  label="Ender 3 Case Lid PS Cover001"
  Placement = pos=(89,43,-34) rot=(1,0,0;3.14159rad)
FEATURE [Sketcher::SketchObject] Sketch010
  ExternalGeometry = -> [Pad002]
  FullyConstrained = false
  MapMode = 5
  Placement = pos=(0,0,0) rot=(1,0,0;3.14159rad)
  Support = -> [Pad002]
  sketch-geometry (27):
    g0: ArcOfCircle CenterX=29.7369 CenterY=-45.1148 CenterZ=0 NormalX=0 NormalY=0 NormalZ=1 AngleXU=0 Radius=2.5 StartAngle=1.5708 EndAngle=4.71239
    g1: ArcOfCircle CenterX=112.41 CenterY=-45.1148 CenterZ=0 NormalX=0 NormalY=0 NormalZ=1 AngleXU=0 Radius=2.5 StartAngle=4.71239 EndAngle=7.85398
    g2: LineSegment StartX=29.7369 StartY=-47.6148 StartZ=0 EndX=112.41 EndY=-47.6148 EndZ=0
    g3: LineSegment StartX=29.7369 StartY=-42.6148 StartZ=0 EndX=112.41 EndY=-42.6148 EndZ=0
    g4: ArcOfCircle CenterX=126.325 CenterY=-116.001 CenterZ=0 NormalX=0 NormalY=0 NormalZ=1 AngleXU=0 Radius=2.5 StartAngle=1.5708 EndAngle=4.71239
    g5: ArcOfCircle CenterX=197.302 CenterY=-116.001 CenterZ=0 NormalX=0 NormalY=0 NormalZ=1 AngleXU=0 Radius=2.5 StartAngle=4.71239 EndAngle=7.85398
    g6: LineSegment StartX=126.325 StartY=-118.501 StartZ=0 EndX=197.302 EndY=-118.501 EndZ=0
    g7: LineSegment StartX=126.325 StartY=-113.501 StartZ=0 EndX=197.302 EndY=-113.501 EndZ=0
    g8: Circle CenterX=58 CenterY=-84.35 CenterZ=0 NormalX=0 NormalY=0 NormalZ=1 AngleXU=0 Radius=2.5
    g9: Circle CenterX=58 CenterY=-84.35 CenterZ=0 NormalX=0 NormalY=0 NormalZ=1 AngleXU=0 Radius=5
    g10: Circle CenterX=108 CenterY=-84.35 CenterZ=0 NormalX=0 NormalY=0 NormalZ=1 AngleXU=0 Radius=2.5
    g11: Circle CenterX=108 CenterY=-84.35 CenterZ=0 NormalX=0 NormalY=0 NormalZ=1 AngleXU=0 Radius=5
    g12: LineSegment StartX=58 StartY=-84.35 StartZ=0 EndX=108 EndY=-84.35 EndZ=0
    g13: Circle CenterX=58 CenterY=-134.35 CenterZ=0 NormalX=0 NormalY=0 NormalZ=1 AngleXU=0 Radius=2.5
    g14: Circle CenterX=58 CenterY=-134.35 CenterZ=0 NormalX=0 NormalY=0 NormalZ=1 AngleXU=0 Radius=5
    g15: LineSegment StartX=58 StartY=-84.35 StartZ=0 EndX=58 EndY=-134.35 EndZ=0
    g16: Circle CenterX=108 CenterY=-134.35 CenterZ=0 NormalX=0 NormalY=0 NormalZ=1 AngleXU=0 Radius=2.5
    g17: Circle CenterX=108 CenterY=-134.35 CenterZ=0 NormalX=0 NormalY=0 NormalZ=1 AngleXU=0 Radius=5
    g18: LineSegment StartX=58 StartY=-134.35 StartZ=0 EndX=108 EndY=-134.35 EndZ=0
    g19: Circle CenterX=132 CenterY=-25 CenterZ=0 NormalX=0 NormalY=0 NormalZ=1 AngleXU=0 Radius=5
    g20: Circle CenterX=132 CenterY=-25 CenterZ=0 NormalX=0 NormalY=0 NormalZ=1 AngleXU=0 Radius=2.5
    g21: Circle CenterX=182 CenterY=-25 CenterZ=0 NormalX=0 NormalY=0 NormalZ=1 AngleXU=0 Radius=2.5
    g22: Circle CenterX=182 CenterY=-25 CenterZ=0 NormalX=0 NormalY=0 NormalZ=1 AngleXU=0 Radius=5
    g23: Circle CenterX=132 CenterY=-75 CenterZ=0 NormalX=0 NormalY=0 NormalZ=1 AngleXU=0 Radius=2.5
    g24: Circle CenterX=132 CenterY=-75 CenterZ=0 NormalX=0 NormalY=0 NormalZ=1 AngleXU=0 Radius=5
    g25: Circle CenterX=182 CenterY=-75 CenterZ=0 NormalX=0 NormalY=0 NormalZ=1 AngleXU=0 Radius=2.5
    g26: Circle CenterX=182 CenterY=-75 CenterZ=0 NormalX=0 NormalY=0 NormalZ=1 AngleXU=0 Radius=5
  constraints (49):
    c: Tangent(g0,g3) = 1.5708
    c: Tangent(g0,g2) = -1.5708
    c: Tangent(g2,g1) = -1.5708
    c: Tangent(g3,g1) = 1.5708
    c: Horizontal(g2)
    c: Equal(g0,g1)
    c: Tangent(g4,g7) = 1.5708
    c: Tangent(g4,g6) = -1.5708
    c: Tangent(g6,g5) = -1.5708
    c: Tangent(g7,g5) = 1.5708
    c: Horizontal(g6)
    c: Equal(g4,g5)
    c: DistanceY(g4,g4) = 5
    c: DistanceY(g1,g1) = 5
    c: Coincident(g8,g-5)
    c: Coincident(g9,g8)
    c: Radius(g9) = 5
    c: Radius(g8) = 2.5
    c: Coincident(g11,g10)
    c: Radius(g11) = 5
    c: Radius(g10) = 2.5
    c: Coincident(g8,g12)
    c: Coincident(g10,g12)
    c: Distance(g12) = 50
    c: Angle(g12) = 0
    c: Coincident(g14,g13)
    c: Radius(g14) = 5
    c: Radius(g13) = 2.5
    c: Coincident(g8,g15)
    c: Coincident(g13,g15)
    c: Equal(g15,g12)
    c: Perpendicular(g15,g12)
    c: Coincident(g17,g16)
    c: Radius(g17) = 5
    c: Radius(g16) = 2.5
    c: Coincident(g13,g18)
    c: Coincident(g16,g18)
    c: Equal(g12,g18)
    c: Parallel(g18,g12)
    c: Coincident(g19,g20)
    c: Equal(g9,g19) = 5
    c: Equal(g8,g20) = 2.5
    c: Coincident(g20,g-9)
    c: Coincident(g22,g21)
    c: Coincident(g22,g-10)
    c: Coincident(g24,g23)
    c: Coincident(g24,g-8)
    c: Coincident(g26,g25)
    c: Coincident(g26,g-3)
FEATURE [PartDesign::Pad] Pad004
  BaseFeature = -> Pad002
  Direction = (1,1,1)
  Length = 6
  Length2 = 100
  Profile = -> Sketch010
  Type = 0
FEATURE [PartDesign::Fillet] Fillet
  Base = -> Pad004 [Edge15,Face49,Edge43,Face58]
  BaseFeature = -> Pad004
  Radius = 2
  SupportTransform = false
FEATURE [PartDesign::Body] Body001  label="Case Lid"
  Group = -> [Sketch008,ShapeBinder,Pad002,Sketch010,Pad004,Fillet]
  Origin = -> Origin001
  Placement = pos=(0,0,55) rot=(0,0,1;0rad)
  Tip = -> Fillet
FEATURE [Part::FeaturePython] Screw008  label="M3x8-Screw"  # Fasteners workbench fastener (typed FeaturePython)
  Placement = pos=(173,66,55) rot=(0,0,1;0rad)
  baseObject = -> Body001 [Edge18]
  diameter = 4
  invert = false
  length = 10
  lengthCustom = 8
  matchOuter = false
  offset = 0
  thread = false
  type = 33
FEATURE [Part::FeaturePython] Screw012  label="M3x8-Screw483"  # Fasteners workbench fastener (typed FeaturePython)
  Placement = pos=(132,75,55) rot=(-1,0,0;3.14159rad)
  baseObject = -> Body001 [Edge30]
  diameter = 4
  invert = false
  length = 10
  lengthCustom = 8
  matchOuter = false
  offset = 0
  thread = false
  type = 33
FEATURE [Part::FeaturePython] Screw013  label="M3x8-Screw484"  # Fasteners workbench fastener (typed FeaturePython)
  Placement = pos=(126.325,116.001,55) rot=(-1,0,0;3.14159rad)
  baseObject = -> Body001 [Edge36]
  diameter = 4
  invert = false
  length = 10
  lengthCustom = 8
  matchOuter = false
  offset = 0
  thread = false
  type = 33
FEATURE [Part::FeaturePython] Screw014  label="M3x8-Screw485"  # Fasteners workbench fastener (typed FeaturePython)
  Placement = pos=(120,143,55) rot=(0,0,1;0rad)
  baseObject = -> Body001 [Edge33]
  diameter = 4
  invert = false
  length = 10
  lengthCustom = 8
  matchOuter = false
  offset = 0
  thread = false
  type = 33
FEATURE [Part::FeaturePython] Screw015  label="M3x8-Screw486"  # Fasteners workbench fastener (typed FeaturePython)
  Placement = pos=(108,84.35,55) rot=(-1,0,0;3.14159rad)
  baseObject = -> Body001 [Edge21]
  diameter = 4
  invert = false
  length = 10
  lengthCustom = 8
  matchOuter = false
  offset = 0
  thread = false
  type = 33
FEATURE [App::DocumentObjectGroup] Group005  label="Case Lid Screws"
  Group = -> [Screw008,Screw012,Screw013,Screw014,Screw015]
FEATURE [App::DocumentObjectGroup] Group004  label="Case Lid Group"
  Group = -> [Body001,Group005]
FEATURE [App::LinkGroup] LinkGroup  label="Assembly"
  ElementList = -> [Body,Part__Feature1009,Group001,Group,Group002,Group003,Group004]
  LinkMode = 0
  Placement = pos=(-1.52588e-05,31.3354,23.5) rot=(1,0,0;3.14159rad)
